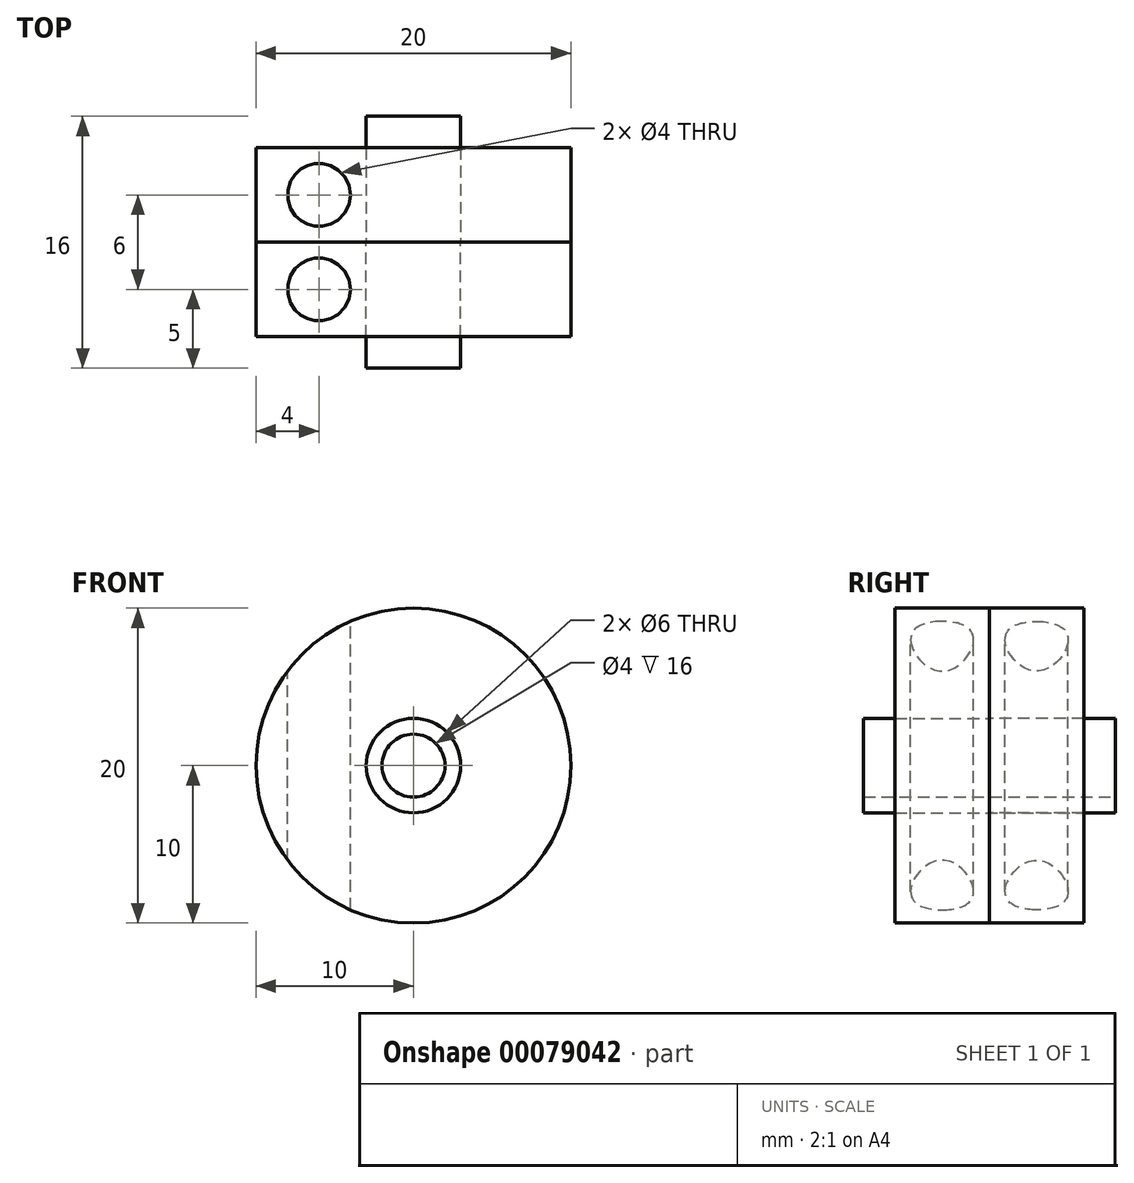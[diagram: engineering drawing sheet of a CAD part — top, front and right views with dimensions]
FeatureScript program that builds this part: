
annotation { "Feature Type Name" : "Feature", "Feature Type Description" : "" }
export const myFeature = defineFeature(function(context is Context, id is Id, definition is map)
    precondition{}
    {
        {
            var Q0;
            Q0=qCreatedBy(makeId("Front.planeOp"),FACE);
            var sketch = newSketch(context, id + "F0", { "sketchPlane" : qUnion([Q0])});
            skCircle(sketch, "E0", {"center": v(0, 0) * mm, "radius": 2 * mm});
            skCircle(sketch, "E1", {"center": v(0, 0) * mm, "radius": 3 * mm});
            skSolve(sketch);
        }
        {
            var Q0;
            Q0=makeQuery(id+"F0.imprint","IMPRINT",FACE,{"disambiguationData":[TD([[makeQuery(id+"F0.imprint","IMPRINT",EDGE,{"derivedFrom":sQuery(id+"F0.wireOp",EDGE,"E0")}),-1.0]])]});
            extrude(context, id + "F1", {"entities" : qUnion([Q0]), "endBound" : BoundingType.SYMMETRIC, "depth" : 16 * mm});
        }
        {
            var Q0;
            Q0=qCreatedBy(makeId("Front.planeOp"),FACE);
            var sketch = newSketch(context, id + "F2", { "sketchPlane" : qUnion([Q0])});
            skCircle(sketch, "E2.0.0", {"center": v(0, 0) * mm, "radius": 3 * mm});
            skCircle(sketch, "E3", {"center": v(0, 0) * mm, "radius": 10 * mm});
            skSolve(sketch);
        }
        {
            var Q0;
            Q0=makeQuery(id+"F2.imprint","IMPRINT",FACE,{"disambiguationData":[TD([[makeQuery(id+"F2.imprint","IMPRINT",EDGE,{"derivedFrom":sQuery(id+"F2.wireOp",EDGE,"E2.0.0")}),-1.0]])]});
            extrude(context, id + "F3", {"entities" : qUnion([Q0]), "depth" : 6 * mm});
        }
        {
            var Q0;
            Q0=makeQuery(id+"F3.opExtrude","CAP_FACE",FACE,{"disambiguationData":[OSD([sQuery(id+"F2.wireOp",EDGE,"E2.0.0"),sQuery(id+"F2.wireOp",EDGE,"E3")])],"isStart":true});
            extrude(context, id + "F4", {"entities" : qUnion([Q0]), "depth" : 6 * mm});
        }
        {
            var Q0;
            Q0=qCreatedBy(makeId("Top.planeOp"),FACE);
            var sketch = newSketch(context, id + "F5", { "sketchPlane" : qUnion([Q0])});
            skLineSegment(sketch, "E4.0", {"start": v(10, -6) * mm, "end": v(-10, -6) * mm, "construction": true});
            skLineSegment(sketch, "E4.1", {"start": v(10, 0) * mm, "end": v(-10, 0) * mm, "construction": true});
            skLineSegment(sketch, "E4.2", {"start": v(10, 6) * mm, "end": v(-10, 6) * mm, "construction": true});
            skLineSegment(sketch, "E5", {"start": v(-10, -6) * mm, "end": v(-10, 6) * mm, "construction": true});
            skLineSegment(sketch, "E6", {"start": v(-6, -6) * mm, "end": v(-6, 6) * mm, "construction": true});
            skPoint(sketch, "E7", {"position": v(-6, 0) * mm});
            skCircle(sketch, "E8", {"center": v(-6, -3) * mm, "radius": 2 * mm});
            skCircle(sketch, "E9", {"center": v(-6, 3) * mm, "radius": 2 * mm});
            skSolve(sketch);
        }
        {
            var Q0;
            Q0=makeQuery(id+"F5.imprint","IMPRINT",FACE,{"disambiguationData":[TD([[makeQuery(id+"F5.imprint","IMPRINT",EDGE,{"derivedFrom":sQuery(id+"F5.wireOp",EDGE,"E8")}),1.0]])]});
            var Q1;
            Q1=makeQuery(id+"F5.imprint","IMPRINT",FACE,{"disambiguationData":[TD([[makeQuery(id+"F5.imprint","IMPRINT",EDGE,{"derivedFrom":sQuery(id+"F5.wireOp",EDGE,"E9")}),1.0]])]});
            extrude(context, id + "F6", {"entities" : qUnion([Q0, Q1]), "operationType" : NewBodyOperationType.REMOVE, "endBound" : BoundingType.SYMMETRIC, "oppositeDirection" : true, "depth" : 25 * mm});
        }
    });
